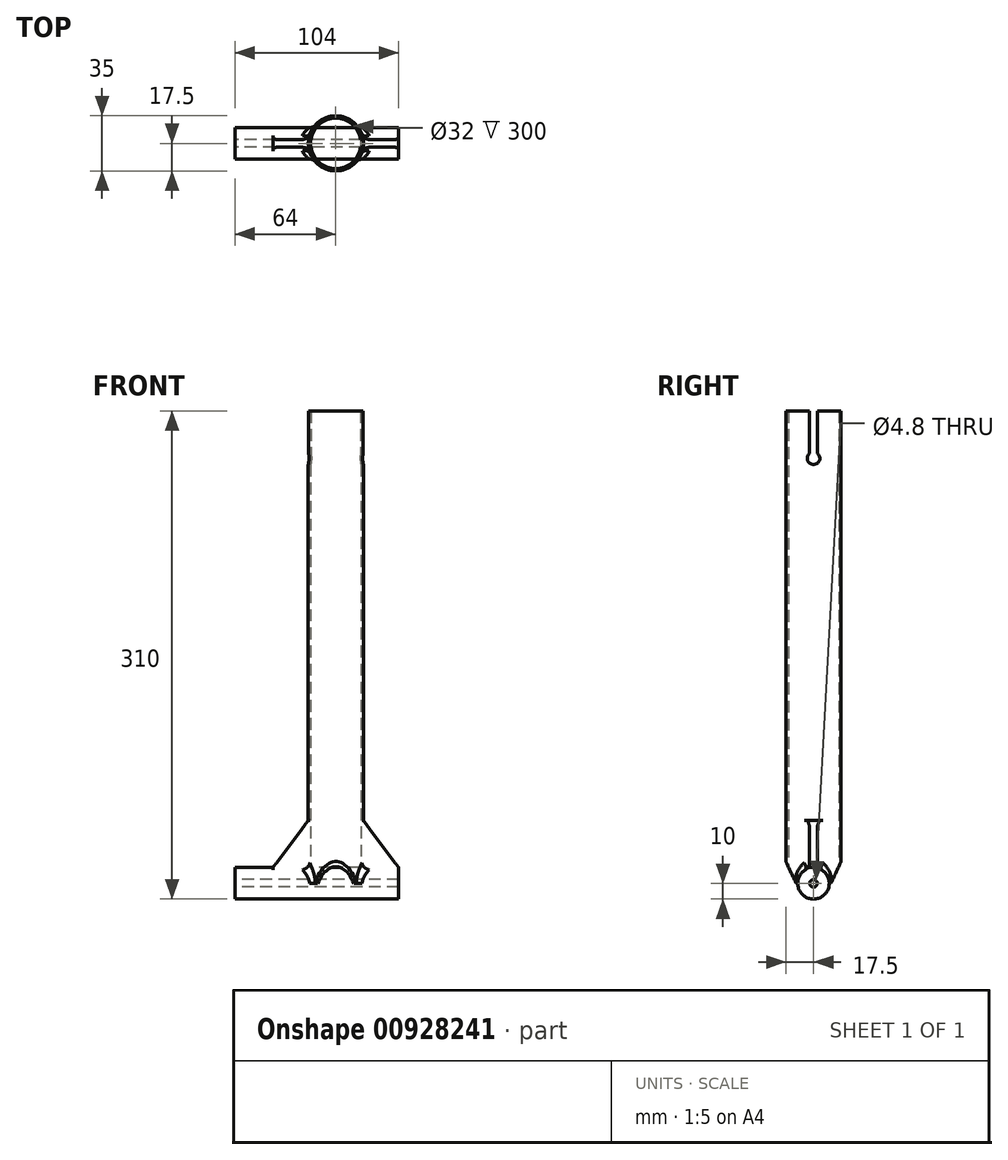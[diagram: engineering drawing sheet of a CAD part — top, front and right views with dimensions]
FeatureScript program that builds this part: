
annotation { "Feature Type Name" : "Feature", "Feature Type Description" : "" }
export const myFeature = defineFeature(function(context is Context, id is Id, definition is map)
    precondition{}
    {
        {
            var Q0;
            Q0=qCreatedBy(makeId("Right.planeOp"),FACE);
            var sketch = newSketch(context, id + "F0", { "sketchPlane" : qUnion([Q0])});
            skCircle(sketch, "E0", {"center": v(0, 0) * mm, "radius": 10 * mm});
            skSolve(sketch);
        }
        {
            var Q0;
            Q0=qCreatedBy(makeId("Top.planeOp"),FACE);
            var sketch = newSketch(context, id + "F1", { "sketchPlane" : qUnion([Q0])});
            skCircle(sketch, "E1", {"center": v(0, 0) * mm, "radius": 17.5 * mm});
            skCircle(sketch, "E2", {"center": v(0, 0) * mm, "radius": 16 * mm});
            skSolve(sketch);
        }
        {
            var Q0;
            Q0=qCreatedBy(makeId("Front.planeOp"),FACE);
            var sketch = newSketch(context, id + "F2", { "sketchPlane" : qUnion([Q0])});
            skLineSegment(sketch, "E3", {"start": v(-40, 9) * mm, "end": v(-16.45, 9) * mm});
            skLineSegment(sketch, "E4", {"start": v(-16.45, 9) * mm, "end": v(-16.45, 40) * mm});
            skLineSegment(sketch, "E5", {"start": v(-16.45, 40) * mm, "end": v(-17.45, 40) * mm});
            skLineSegment(sketch, "E6", {"start": v(-17.45, 40) * mm, "end": v(-40, 10) * mm});
            skLineSegment(sketch, "E7", {"start": v(-40, 10) * mm, "end": v(-40, 9) * mm});
            skLineSegment(sketch, "E8.MirrorCS", {"start": v(17.45, 40) * mm, "end": v(40, 10) * mm});
            skLineSegment(sketch, "E9.MirrorCS", {"start": v(16.45, 40) * mm, "end": v(17.45, 40) * mm});
            skLineSegment(sketch, "E10.MirrorCS", {"start": v(16.45, 9) * mm, "end": v(16.45, 40) * mm});
            skLineSegment(sketch, "E11.MirrorCS", {"start": v(40, 9) * mm, "end": v(16.45, 9) * mm});
            skLineSegment(sketch, "E12.MirrorCS", {"start": v(40, 10) * mm, "end": v(40, 9) * mm});
            skSolve(sketch);
        }
        {
            var Q0;
            Q0=qCreatedBy(makeId("Right.planeOp"),FACE);
            var sketch = newSketch(context, id + "F3", { "sketchPlane" : qUnion([Q0])});
            skArc(sketch, "E13", {"start": v(-9.06, -4.23) * mm, "mid": v(0, -10) * mm, "end": v(9.06, -4.23) * mm});
            skLineSegment(sketch, "E14", {"start": v(9.06, -4.23) * mm, "end": v(21.74, 22.96) * mm});
            skLineSegment(sketch, "E15", {"start": v(-9.06, -4.23) * mm, "end": v(-21.74, 22.96) * mm});
            skLineSegment(sketch, "E16.0", {"start": v(-18.13, -8.45) * mm, "end": v(-30.8, 18.74) * mm});
            skArc(sketch, "E16.1", {"start": v(-18.13, -8.45) * mm, "mid": v(0, -20) * mm, "end": v(18.13, -8.45) * mm});
            skLineSegment(sketch, "E16.2", {"start": v(18.13, -8.45) * mm, "end": v(30.8, 18.74) * mm});
            skLineSegment(sketch, "E17", {"start": v(-30.8, 18.74) * mm, "end": v(-21.74, 22.96) * mm});
            skLineSegment(sketch, "E18", {"start": v(21.74, 22.96) * mm, "end": v(30.8, 18.74) * mm});
            skSolve(sketch);
        }
        {
            var Q0;
            Q0=qCreatedBy(makeId("Right.planeOp"),FACE);
            var sketch = newSketch(context, id + "F4", { "sketchPlane" : qUnion([Q0])});
            skCircle(sketch, "E19", {"center": v(0, 0) * mm, "radius": 2.4 * mm});
            skSolve(sketch);
        }
        {
            var Q0;
            Q0=qCreatedBy(makeId("Right.planeOp"),FACE);
            var sketch = newSketch(context, id + "F5", { "sketchPlane" : qUnion([Q0])});
            skArc(sketch, "E20", {"start": v(-2.5, 273.12) * mm, "mid": v(0, 266) * mm, "end": v(2.5, 273.12) * mm});
            skArc(sketch, "E21.0.endCap", {"start": v(-2.5, 310) * mm, "mid": v(0, 312.5) * mm, "end": v(2.5, 310) * mm});
            skLineSegment(sketch, "E21.0.left", {"start": v(-2.5, 273.12) * mm, "end": v(-2.5, 310) * mm});
            skLineSegment(sketch, "E21.0.right", {"start": v(2.5, 273.12) * mm, "end": v(2.5, 310) * mm});
            skSolve(sketch);
        }
        {
            var Q0;
            Q0=qSketchRegion(id+"F0",true);
            extrude(context, id + "F6", {"entities" : qUnion([Q0]), "depth" : 40 * mm, "offsetDistance" : 25 * mm, "hasSecondDirection" : true, "secondDirectionOppositeDirection" : true, "secondDirectionDepth" : 64 * mm});
        }
        {
            var Q0;
            Q0=qSketchRegion(id+"F1",true);
            extrude(context, id + "F7", {"entities" : qUnion([Q0]), "operationType" : NewBodyOperationType.ADD, "depth" : 300 * mm, "offsetDistance" : 25 * mm});
        }
        {
            var Q0;
            Q0=qSketchRegion(id+"F2",true);
            extrude(context, id + "F8", {"entities" : qUnion([Q0]), "operationType" : NewBodyOperationType.ADD, "endBound" : BoundingType.SYMMETRIC, "depth" : 5 * mm, "offsetDistance" : 25 * mm});
        }
        {
            var Q0;
            Q0=qSketchRegion(id+"F3",true);
            extrude(context, id + "F9", {"entities" : qUnion([Q0]), "operationType" : NewBodyOperationType.REMOVE, "endBound" : BoundingType.SYMMETRIC, "depth" : 80 * mm, "offsetDistance" : 25 * mm});
        }
        {
            var Q0;
            Q0=qSketchRegion(id+"F4",true);
            extrude(context, id + "F10", {"entities" : qUnion([Q0]), "operationType" : NewBodyOperationType.REMOVE, "endBound" : BoundingType.THROUGH_ALL, "depth" : 80 * mm, "offsetDistance" : 25 * mm, "hasSecondDirection" : true, "secondDirectionBound" : SecondDirectionBoundingType.THROUGH_ALL, "secondDirectionOppositeDirection" : true, "secondDirectionDepth" : 25 * mm});
        }
        {
            var Q0;
            Q0=makeQuery(id+"F8.boolean.opBoolean","INTERSECT",EDGE,{"derivedFrom":[makeQuery(id+"F7.opExtrude","SWEPT_FACE",FACE,{"disambiguationData":[OSD([sQuery(id+"F1.wireOp",EDGE,"E1")])]}),makeQuery(id+"F8.opExtrude","CAP_FACE",FACE,{"disambiguationData":[OSD([sQuery(id+"F2.wireOp",EDGE,"E8.MirrorCS"),sQuery(id+"F2.wireOp",EDGE,"E9.MirrorCS"),sQuery(id+"F2.wireOp",EDGE,"E10.MirrorCS"),sQuery(id+"F2.wireOp",EDGE,"E11.MirrorCS"),sQuery(id+"F2.wireOp",EDGE,"E12.MirrorCS")])],"isStart":false})]});
            var Q1;
            Q1=makeQuery(id+"F8.boolean.opBoolean","INTERSECT",EDGE,{"derivedFrom":[makeQuery(id+"F6.opExtrude","SWEPT_FACE",FACE,{"disambiguationData":[OSD([sQuery(id+"F0.wireOp",EDGE,"E0")])]}),makeQuery(id+"F8.opExtrude","CAP_FACE",FACE,{"disambiguationData":[OSD([sQuery(id+"F2.wireOp",EDGE,"E8.MirrorCS"),sQuery(id+"F2.wireOp",EDGE,"E9.MirrorCS"),sQuery(id+"F2.wireOp",EDGE,"E10.MirrorCS"),sQuery(id+"F2.wireOp",EDGE,"E11.MirrorCS"),sQuery(id+"F2.wireOp",EDGE,"E12.MirrorCS")])],"isStart":false})]});
            var Q2;
            Q2=makeQuery(id+"F8.boolean.opBoolean","INTERSECT",EDGE,{"derivedFrom":[makeQuery(id+"F7.opExtrude","SWEPT_FACE",FACE,{"disambiguationData":[OSD([sQuery(id+"F1.wireOp",EDGE,"E1")])]}),makeQuery(id+"F8.opExtrude","CAP_FACE",FACE,{"disambiguationData":[OSD([sQuery(id+"F2.wireOp",EDGE,"E8.MirrorCS"),sQuery(id+"F2.wireOp",EDGE,"E9.MirrorCS"),sQuery(id+"F2.wireOp",EDGE,"E10.MirrorCS"),sQuery(id+"F2.wireOp",EDGE,"E11.MirrorCS"),sQuery(id+"F2.wireOp",EDGE,"E12.MirrorCS")])],"isStart":true})]});
            var Q3;
            Q3=makeQuery(id+"F8.boolean.opBoolean","INTERSECT",EDGE,{"derivedFrom":[makeQuery(id+"F6.opExtrude","SWEPT_FACE",FACE,{"disambiguationData":[OSD([sQuery(id+"F0.wireOp",EDGE,"E0")])]}),makeQuery(id+"F8.opExtrude","CAP_FACE",FACE,{"disambiguationData":[OSD([sQuery(id+"F2.wireOp",EDGE,"E8.MirrorCS"),sQuery(id+"F2.wireOp",EDGE,"E9.MirrorCS"),sQuery(id+"F2.wireOp",EDGE,"E10.MirrorCS"),sQuery(id+"F2.wireOp",EDGE,"E11.MirrorCS"),sQuery(id+"F2.wireOp",EDGE,"E12.MirrorCS")])],"isStart":true})]});
            var Q4;
            Q4=makeQuery(id+"F8.boolean.opBoolean","INTERSECT",EDGE,{"derivedFrom":[makeQuery(id+"F6.opExtrude","SWEPT_FACE",FACE,{"disambiguationData":[OSD([sQuery(id+"F0.wireOp",EDGE,"E0")])]}),makeQuery(id+"F8.opExtrude","CAP_FACE",FACE,{"disambiguationData":[OSD([sQuery(id+"F2.wireOp",EDGE,"E3"),sQuery(id+"F2.wireOp",EDGE,"E4"),sQuery(id+"F2.wireOp",EDGE,"E5"),sQuery(id+"F2.wireOp",EDGE,"E6"),sQuery(id+"F2.wireOp",EDGE,"E7")])],"isStart":true})]});
            var Q5;
            Q5=makeQuery(id+"F8.boolean.opBoolean","INTERSECT",EDGE,{"derivedFrom":[makeQuery(id+"F7.opExtrude","SWEPT_FACE",FACE,{"disambiguationData":[OSD([sQuery(id+"F1.wireOp",EDGE,"E1")])]}),makeQuery(id+"F8.opExtrude","CAP_FACE",FACE,{"disambiguationData":[OSD([sQuery(id+"F2.wireOp",EDGE,"E3"),sQuery(id+"F2.wireOp",EDGE,"E4"),sQuery(id+"F2.wireOp",EDGE,"E5"),sQuery(id+"F2.wireOp",EDGE,"E6"),sQuery(id+"F2.wireOp",EDGE,"E7")])],"isStart":true})]});
            var Q6;
            Q6=makeQuery(id+"F8.boolean.opBoolean","INTERSECT",EDGE,{"derivedFrom":[makeQuery(id+"F7.opExtrude","SWEPT_FACE",FACE,{"disambiguationData":[OSD([sQuery(id+"F1.wireOp",EDGE,"E1")])]}),makeQuery(id+"F8.opExtrude","CAP_FACE",FACE,{"disambiguationData":[OSD([sQuery(id+"F2.wireOp",EDGE,"E3"),sQuery(id+"F2.wireOp",EDGE,"E4"),sQuery(id+"F2.wireOp",EDGE,"E5"),sQuery(id+"F2.wireOp",EDGE,"E6"),sQuery(id+"F2.wireOp",EDGE,"E7")])],"isStart":false})]});
            var Q7;
            Q7=makeQuery(id+"F8.boolean.opBoolean","INTERSECT",EDGE,{"derivedFrom":[makeQuery(id+"F6.opExtrude","SWEPT_FACE",FACE,{"disambiguationData":[OSD([sQuery(id+"F0.wireOp",EDGE,"E0")])]}),makeQuery(id+"F8.opExtrude","CAP_FACE",FACE,{"disambiguationData":[OSD([sQuery(id+"F2.wireOp",EDGE,"E3"),sQuery(id+"F2.wireOp",EDGE,"E4"),sQuery(id+"F2.wireOp",EDGE,"E5"),sQuery(id+"F2.wireOp",EDGE,"E6"),sQuery(id+"F2.wireOp",EDGE,"E7")])],"isStart":false})]});
            var Q8;
            {var subQ0=makeQuery(id+"F6.opExtrude","SWEPT_FACE",FACE,{"disambiguationData":[OSD([sQuery(id+"F0.wireOp",EDGE,"E0")])]});var subQ1=sQuery(id+"F1.wireOp",EDGE,"E1");var subQ2=makeQuery(id+"F7.opExtrude","SWEPT_FACE",FACE,{"disambiguationData":[OSD([subQ1])]});Q8=makeQuery(id+"F8.boolean.opBoolean","SPLIT",EDGE,{"disambiguationData":[TD([makeQuery(id+"F8.opExtrude","CAP_FACE",FACE,{"disambiguationData":[OSD([sQuery(id+"F2.wireOp",EDGE,"E3"),sQuery(id+"F2.wireOp",EDGE,"E4"),sQuery(id+"F2.wireOp",EDGE,"E5"),sQuery(id+"F2.wireOp",EDGE,"E6"),sQuery(id+"F2.wireOp",EDGE,"E7")])],"isStart":true})])],"derivedFrom":makeQuery(id+"F7.boolean.opBoolean","INTERSECT",EDGE,{"disambiguationData":[OD(0.0)],"derivedFrom":[subQ0,subQ2]})});}
            var Q9;
            {var subQ0=makeQuery(id+"F6.opExtrude","SWEPT_FACE",FACE,{"disambiguationData":[OSD([sQuery(id+"F0.wireOp",EDGE,"E0")])]});var subQ1=sQuery(id+"F1.wireOp",EDGE,"E1");var subQ2=makeQuery(id+"F7.opExtrude","SWEPT_FACE",FACE,{"disambiguationData":[OSD([subQ1])]});Q9=makeQuery(id+"F8.boolean.opBoolean","SPLIT",EDGE,{"disambiguationData":[TD([makeQuery(id+"F8.opExtrude","CAP_FACE",FACE,{"disambiguationData":[OSD([sQuery(id+"F2.wireOp",EDGE,"E8.MirrorCS"),sQuery(id+"F2.wireOp",EDGE,"E9.MirrorCS"),sQuery(id+"F2.wireOp",EDGE,"E10.MirrorCS"),sQuery(id+"F2.wireOp",EDGE,"E11.MirrorCS"),sQuery(id+"F2.wireOp",EDGE,"E12.MirrorCS")])],"isStart":true})])],"derivedFrom":makeQuery(id+"F7.boolean.opBoolean","INTERSECT",EDGE,{"disambiguationData":[OD(1.0)],"derivedFrom":[subQ0,subQ2]})});}
            var Q10;
            {var subQ0=makeQuery(id+"F6.opExtrude","SWEPT_FACE",FACE,{"disambiguationData":[OSD([sQuery(id+"F0.wireOp",EDGE,"E0")])]});var subQ1=sQuery(id+"F1.wireOp",EDGE,"E1");var subQ2=makeQuery(id+"F7.opExtrude","SWEPT_FACE",FACE,{"disambiguationData":[OSD([subQ1])]});Q10=makeQuery(id+"F8.boolean.opBoolean","SPLIT",EDGE,{"disambiguationData":[TD([makeQuery(id+"F8.opExtrude","CAP_FACE",FACE,{"disambiguationData":[OSD([sQuery(id+"F2.wireOp",EDGE,"E8.MirrorCS"),sQuery(id+"F2.wireOp",EDGE,"E9.MirrorCS"),sQuery(id+"F2.wireOp",EDGE,"E10.MirrorCS"),sQuery(id+"F2.wireOp",EDGE,"E11.MirrorCS"),sQuery(id+"F2.wireOp",EDGE,"E12.MirrorCS")])],"isStart":false})])],"derivedFrom":makeQuery(id+"F7.boolean.opBoolean","INTERSECT",EDGE,{"disambiguationData":[OD(1.0)],"derivedFrom":[subQ0,subQ2]})});}
            var Q11;
            {var subQ0=makeQuery(id+"F6.opExtrude","SWEPT_FACE",FACE,{"disambiguationData":[OSD([sQuery(id+"F0.wireOp",EDGE,"E0")])]});var subQ1=sQuery(id+"F1.wireOp",EDGE,"E1");var subQ2=makeQuery(id+"F7.opExtrude","SWEPT_FACE",FACE,{"disambiguationData":[OSD([subQ1])]});Q11=makeQuery(id+"F8.boolean.opBoolean","SPLIT",EDGE,{"disambiguationData":[TD([makeQuery(id+"F8.opExtrude","CAP_FACE",FACE,{"disambiguationData":[OSD([sQuery(id+"F2.wireOp",EDGE,"E3"),sQuery(id+"F2.wireOp",EDGE,"E4"),sQuery(id+"F2.wireOp",EDGE,"E5"),sQuery(id+"F2.wireOp",EDGE,"E6"),sQuery(id+"F2.wireOp",EDGE,"E7")])],"isStart":false})])],"derivedFrom":makeQuery(id+"F7.boolean.opBoolean","INTERSECT",EDGE,{"disambiguationData":[OD(0.0)],"derivedFrom":[subQ0,subQ2]})});}
            fillet(context, id + "F11", {"entities" : qUnion([Q0, Q1, Q2, Q3, Q4, Q5, Q6, Q7, Q8, Q9, Q10, Q11]), "radius" : 5 * mm, "tangentPropagation" : true});
        }
        {
            var Q0;
            Q0=qSketchRegion(id+"F5",true);
            extrude(context, id + "F12", {"entities" : qUnion([Q0]), "operationType" : NewBodyOperationType.REMOVE, "endBound" : BoundingType.SYMMETRIC, "depth" : 50 * mm, "offsetDistance" : 25 * mm});
        }
    });
